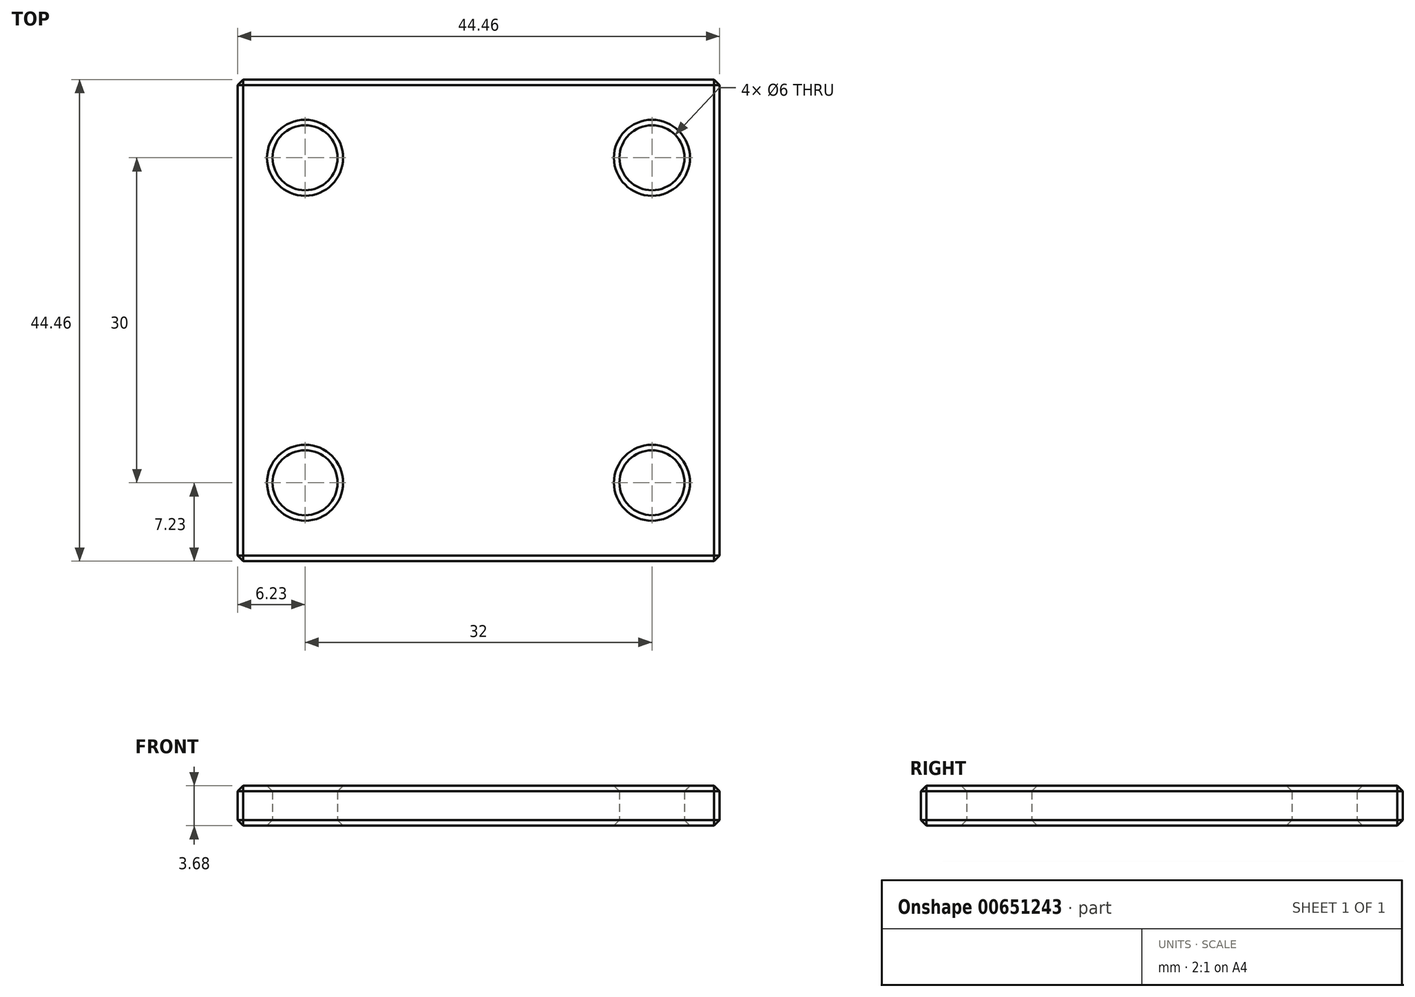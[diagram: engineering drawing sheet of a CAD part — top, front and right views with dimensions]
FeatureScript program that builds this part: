
annotation { "Feature Type Name" : "Feature", "Feature Type Description" : "" }
export const myFeature = defineFeature(function(context is Context, id is Id, definition is map)
    precondition{}
    {
        {
            var Q0;
            Q0=qCreatedBy(makeId("Top.planeOp"),FACE);
            var sketch = newSketch(context, id + "F0", { "sketchPlane" : qUnion([Q0])});
            skPoint(sketch, "E0.middle", {"position": v(0, 0) * mm});
            skLineSegment(sketch, "E1.bottom", {"start": v(22.22, -22.22) * mm, "end": v(-22.23, -22.23) * mm});
            skLineSegment(sketch, "E1.top", {"start": v(22.23, 22.23) * mm, "end": v(-22.23, 22.22) * mm});
            skLineSegment(sketch, "E1.left", {"start": v(22.22, -22.23) * mm, "end": v(22.23, 22.23) * mm});
            skLineSegment(sketch, "E1.right", {"start": v(-22.23, -22.23) * mm, "end": v(-22.23, 22.22) * mm});
            skCircle(sketch, "E2", {"center": v(-16, 15) * mm, "radius": 3 * mm});
            skCircle(sketch, "E3", {"center": v(-16, -15) * mm, "radius": 3 * mm});
            skCircle(sketch, "E4", {"center": v(16, -15) * mm, "radius": 3 * mm});
            skCircle(sketch, "E5", {"center": v(16, 15) * mm, "radius": 3 * mm});
            skSolve(sketch);
        }
        {
            var Q0;
            Q0=makeQuery(id+"F0.imprint","IMPRINT",FACE,{"disambiguationData":[TD([[makeQuery(id+"F0.imprint","IMPRINT",EDGE,{"derivedFrom":sQuery(id+"F0.wireOp",EDGE,"E1.bottom")}),-1.0]])]});
            extrude(context, id + "F1", {"entities" : qUnion([Q0]), "depth" : 3.68 * mm, "offsetDistance" : 25.4 * mm});
        }
        {
            var Q0;
            Q0=makeQuery(id+"F1.opExtrude","CAP_EDGE",EDGE,{"disambiguationData":[OSD([sQuery(id+"F0.wireOp",EDGE,"E2")])],"isStart":false});
            var Q1;
            Q1=makeQuery(id+"F1.opExtrude","CAP_EDGE",EDGE,{"disambiguationData":[OSD([sQuery(id+"F0.wireOp",EDGE,"E5")])],"isStart":false});
            var Q2;
            Q2=makeQuery(id+"F1.opExtrude","CAP_EDGE",EDGE,{"disambiguationData":[OSD([sQuery(id+"F0.wireOp",EDGE,"E3")])],"isStart":false});
            var Q3;
            Q3=makeQuery(id+"F1.opExtrude","SWEPT_FACE",FACE,{"disambiguationData":[OSD([sQuery(id+"F0.wireOp",EDGE,"E4")])]});
            var Q4;
            Q4=makeQuery(id+"F1.opExtrude","CAP_EDGE",EDGE,{"disambiguationData":[OSD([sQuery(id+"F0.wireOp",EDGE,"E3")])],"isStart":true});
            var Q5;
            Q5=makeQuery(id+"F1.opExtrude","CAP_EDGE",EDGE,{"disambiguationData":[OSD([sQuery(id+"F0.wireOp",EDGE,"E5")])],"isStart":true});
            var Q6;
            Q6=makeQuery(id+"F1.opExtrude","CAP_EDGE",EDGE,{"disambiguationData":[OSD([sQuery(id+"F0.wireOp",EDGE,"E2")])],"isStart":true});
            var Q7;
            Q7=makeQuery(id+"F1.opExtrude","CAP_FACE",FACE,{"disambiguationData":[OSD([sQuery(id+"F0.wireOp",EDGE,"E1.bottom"),sQuery(id+"F0.wireOp",EDGE,"E1.top"),sQuery(id+"F0.wireOp",EDGE,"E1.left"),sQuery(id+"F0.wireOp",EDGE,"E1.right"),sQuery(id+"F0.wireOp",EDGE,"E2"),sQuery(id+"F0.wireOp",EDGE,"E3"),sQuery(id+"F0.wireOp",EDGE,"E4"),sQuery(id+"F0.wireOp",EDGE,"E5")])],"isStart":true});
            var Q8;
            Q8=makeQuery(id+"F1.opExtrude","SWEPT_FACE",FACE,{"disambiguationData":[OSD([sQuery(id+"F0.wireOp",EDGE,"E1.right")])]});
            var Q9;
            Q9=makeQuery(id+"F1.opExtrude","SWEPT_FACE",FACE,{"disambiguationData":[OSD([sQuery(id+"F0.wireOp",EDGE,"E1.top")])]});
            var Q10;
            Q10=makeQuery(id+"F1.opExtrude","SWEPT_FACE",FACE,{"disambiguationData":[OSD([sQuery(id+"F0.wireOp",EDGE,"E1.left")])]});
            var Q11;
            Q11=makeQuery(id+"F1.opExtrude","SWEPT_FACE",FACE,{"disambiguationData":[OSD([sQuery(id+"F0.wireOp",EDGE,"E1.bottom")])]});
            chamfer(context, id + "F2", {"entities" : qUnion([Q0, Q1, Q2, Q3, Q4, Q5, Q6, Q7, Q8, Q9, Q10, Q11]), "width" : 0.5 * mm, "tangentPropagation" : true});
        }
    });
